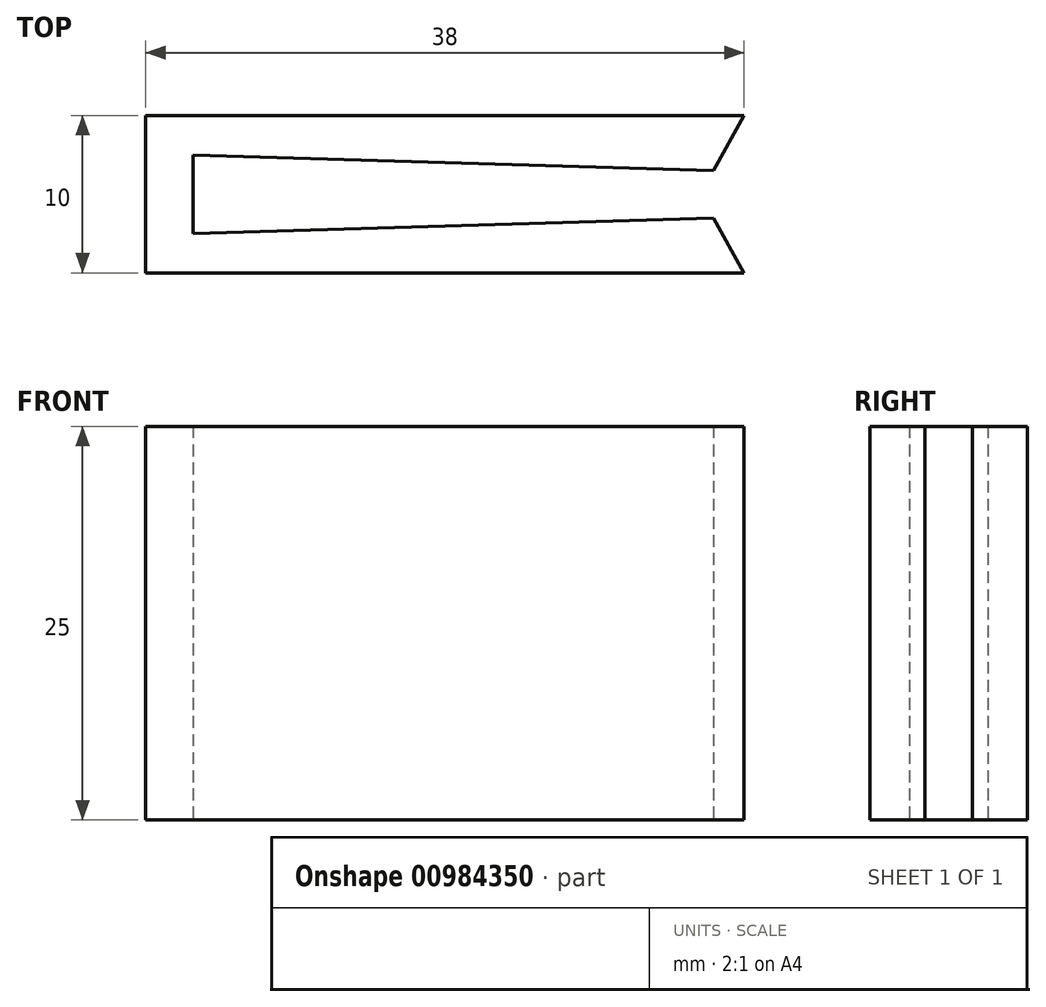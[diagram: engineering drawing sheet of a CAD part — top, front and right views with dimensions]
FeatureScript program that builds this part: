
annotation { "Feature Type Name" : "Feature", "Feature Type Description" : "" }
export const myFeature = defineFeature(function(context is Context, id is Id, definition is map)
    precondition{}
    {
        {
            var Q0;
            Q0=qCreatedBy(makeId("Top.planeOp"),FACE);
            var sketch = newSketch(context, id + "F0", { "sketchPlane" : qUnion([Q0])});
            skLineSegment(sketch, "E0", {"start": v(11.72, 6.5) * mm, "end": v(-26.28, 6.5) * mm});
            skLineSegment(sketch, "E1", {"start": v(-26.28, 6.5) * mm, "end": v(-26.28, -3.5) * mm});
            skLineSegment(sketch, "E2", {"start": v(-26.28, -3.5) * mm, "end": v(11.72, -3.5) * mm});
            skLineSegment(sketch, "E3", {"start": v(11.72, -3.5) * mm, "end": v(9.79, 0) * mm});
            skLineSegment(sketch, "E4", {"start": v(9.79, 0) * mm, "end": v(-23.28, -1) * mm});
            skLineSegment(sketch, "E5", {"start": v(-23.28, -1) * mm, "end": v(-23.28, 4) * mm});
            skLineSegment(sketch, "E6", {"start": v(-23.28, 4) * mm, "end": v(9.79, 3) * mm});
            skLineSegment(sketch, "E7", {"start": v(9.79, 3) * mm, "end": v(11.72, 6.5) * mm});
            skSolve(sketch);
        }
        {
            var Q0;
            Q0=makeQuery(id+"F0.imprint","IMPRINT",FACE,{"disambiguationData":[TD([[makeQuery(id+"F0.imprint","IMPRINT",EDGE,{"derivedFrom":sQuery(id+"F0.wireOp",EDGE,"E0")}),1.0]])]});
            extrude(context, id + "F1", {"entities" : qUnion([Q0]), "depth" : 25 * mm, "offsetDistance" : 25 * mm});
        }
    });
